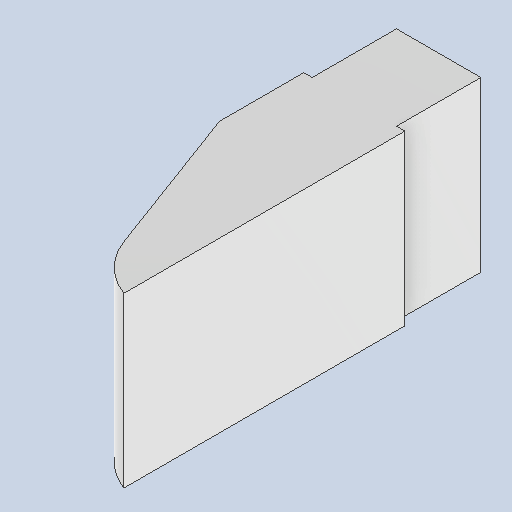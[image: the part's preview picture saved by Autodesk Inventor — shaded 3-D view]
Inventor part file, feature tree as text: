
AUTODESK INVENTOR PART (.ipt)
format: ipt  version: 2025 (Build 290162010, 162A)  size: 137,216 bytes
history: native  units: mm
features: other x6, sketch x2, hole x1, reference x1
ambient origin geometry x8: Origin, YZ Plane, XZ Plane, XY Plane, X Axis, Y Axis, Z Axis, Center Point
bodies: Volumenkörper1 (feature_tree)
feature tree (10):
  other  "MontageAufnahmeLO.ipt"
  hole  "Bohrung1"  [1 undecoded]
  other  "Volumenkörper1::MontageAufnahmeLO.ipt"
  other  "Bezeichnung1"
  sketch  "Skizze1"  dims[d0=10.0mm d1=6.5mm]
  sketch  "Skizze2"  dims[d2=5.0mm d3=1.567mm d4=8.0mm d5=4.0mm d6=2.0mm d7=90.0deg d8=10.0mm d9=20.594885mm]
  reference  "Referenz1"
  other  "<userpath>\Documents\Inventor\Krandemonstrator\Demonstrator.iam"
  other  "Demonstrator.iam"
  other  "Bolt GB/T 798-1988 M4 x 20:4"
note: 1 required parameter value undecoded (feature->parameter linkage not recoverable at this tier; creation-order binding heuristic only, values carry confidence <= 0.55)
